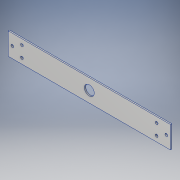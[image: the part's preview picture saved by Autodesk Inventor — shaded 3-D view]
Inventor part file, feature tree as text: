
AUTODESK INVENTOR PART (.ipt)
format: ipt  version: 2017 (Build 210142000, 142)  size: 118,784 bytes
history: native  units: in
note: dims shown in document units (in); Inventor stores cm internally (conversion verified against a paired STEP export)
features: extrude x1, hole x1, sketch x1
ambient origin geometry x8: Origin, YZ Plane, XZ Plane, XY Plane, X Axis, Y Axis, Z Axis, Center Point
bodies: Body1 (feature_tree)
feature tree (3):
  extrude  "Extrusion2"  Depth=0.75in
  hole  "Hole1"  [1 undecoded]
  sketch  "Sketch3"  dims[d0=14.75in d3=0.5in d4=1.0in d5=0.25in d6=0.25in d10=0.25in d11=1.25in d12=0.125in d13=0.0in d14=0.9in d15=0.75in d16=0.375in d17=0.25in d18=0.5635in d19=1.0in d20=0.8108in]
note: 1 required parameter value undecoded (feature->parameter linkage not recoverable at this tier; creation-order binding heuristic only, values carry confidence <= 0.55)
